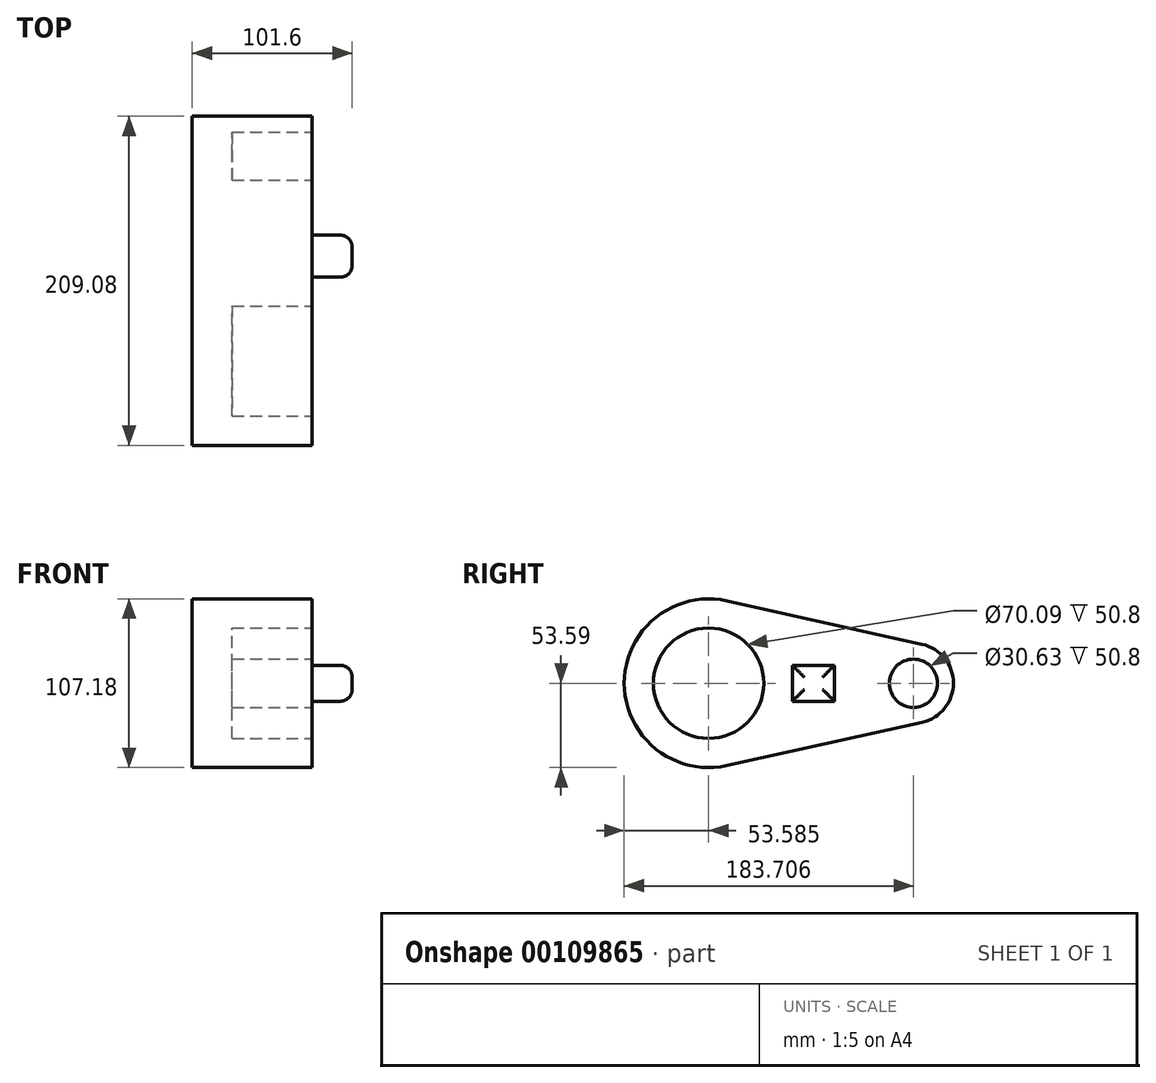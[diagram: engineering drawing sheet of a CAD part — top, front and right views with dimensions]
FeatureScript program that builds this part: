
annotation { "Feature Type Name" : "Feature", "Feature Type Description" : "" }
export const myFeature = defineFeature(function(context is Context, id is Id, definition is map)
    precondition{}
    {
        {
            var Q0;
            Q0=qCreatedBy(makeId("Right.planeOp"),FACE);
            var sketch = newSketch(context, id + "F0", { "sketchPlane" : qUnion([Q0])});
            skCircle(sketch, "E0", {"center": v(-66.59, 0) * mm, "radius": 53.59 * mm});
            skCircle(sketch, "E1", {"center": v(63.5, 0) * mm, "radius": 25.4 * mm});
            skLineSegment(sketch, "E2", {"start": v(-54.97, 52.32) * mm, "end": v(69, 24.8) * mm});
            skLineSegment(sketch, "E3", {"start": v(-54.97, -52.32) * mm, "end": v(69, -24.8) * mm});
            skSolve(sketch);
        }
        {
            var Q0;
            Q0 = qSketchRegion(id + "F0", true);
            extrude(context, id + "F1", {"entities" : qUnion([Q0]), "depth" : 76.2 * mm});
        }
        {
            var Q0;
            Q0=makeQuery(id+"F1.opExtrude","CAP_FACE",FACE,{"disambiguationData":[OSD([sQuery(id+"F0.wireOp",EDGE,"E0"),sQuery(id+"F0.wireOp",EDGE,"E1"),sQuery(id+"F0.wireOp",EDGE,"E2"),sQuery(id+"F0.wireOp",EDGE,"E3")])],"isStart":false});
            var sketch = newSketch(context, id + "F2", { "sketchPlane" : qUnion([Q0])});
            skCircle(sketch, "E4", {"center": v(-66.59, 0) * mm, "radius": 35.04 * mm});
            skSolve(sketch);
        }
        {
            var Q0;
            Q0=makeQuery(id+"F2.imprint","IMPRINT",FACE,{"disambiguationData":[TD([[makeQuery(id+"F2.imprint","IMPRINT",EDGE,{"derivedFrom":sQuery(id+"F2.wireOp",EDGE,"E4")}),1.0]])]});
            extrude(context, id + "F3", {"entities" : qUnion([Q0]), "operationType" : NewBodyOperationType.REMOVE, "oppositeDirection" : true, "depth" : 50.8 * mm});
        }
        {
            var Q0;
            Q0=makeQuery(id+"F2.imprint","IMPRINT",FACE,{"disambiguationData":[TD([[makeQuery(id+"F2.imprint","IMPRINT",EDGE,{"derivedFrom":sQuery(id+"F2.wireOp",EDGE,"E4")}),-1.0]])]});
            var sketch = newSketch(context, id + "F4", { "sketchPlane" : qUnion([Q0])});
            skCircle(sketch, "E5", {"center": v(63.54, 0) * mm, "radius": 15.32 * mm});
            skSolve(sketch);
        }
        {
            var Q0;
            Q0 = qSketchRegion(id + "F4", true);
            extrude(context, id + "F5", {"entities" : qUnion([Q0]), "operationType" : NewBodyOperationType.REMOVE, "oppositeDirection" : true, "depth" : 50.8 * mm});
        }
        {
            var Q0;
            Q0=makeQuery(id+"F2.imprint","IMPRINT",FACE,{"disambiguationData":[TD([[makeQuery(id+"F2.imprint","IMPRINT",EDGE,{"derivedFrom":sQuery(id+"F2.wireOp",EDGE,"E4")}),-1.0]])]});
            var sketch = newSketch(context, id + "F6", { "sketchPlane" : qUnion([Q0])});
            skLineSegment(sketch, "E6.bottom", {"start": v(13.39, -11.46) * mm, "end": v(-13.39, -11.46) * mm});
            skLineSegment(sketch, "E6.top", {"start": v(13.39, 11.46) * mm, "end": v(-13.39, 11.46) * mm});
            skLineSegment(sketch, "E6.left", {"start": v(13.39, -11.46) * mm, "end": v(13.39, 11.46) * mm});
            skLineSegment(sketch, "E6.right", {"start": v(-13.39, -11.46) * mm, "end": v(-13.39, 11.46) * mm});
            skPoint(sketch, "E6.middle", {"position": v(0, 0) * mm});
            skSolve(sketch);
        }
        {
            var Q0;
            Q0 = qSketchRegion(id + "F6", true);
            extrude(context, id + "F7", {"entities" : qUnion([Q0]), "operationType" : NewBodyOperationType.ADD, "depth" : 25.4 * mm});
        }
        {
            var Q0;
            Q0=makeQuery(id+"F7.opExtrude","CAP_FACE",FACE,{"disambiguationData":[OSD([sQuery(id+"F6.wireOp",EDGE,"E6.bottom"),sQuery(id+"F6.wireOp",EDGE,"E6.top"),sQuery(id+"F6.wireOp",EDGE,"E6.left"),sQuery(id+"F6.wireOp",EDGE,"E6.right")])],"isStart":false});
            fillet(context, id + "F8", {"entities" : qUnion([Q0]), "radius" : 7.62 * mm, "tangentPropagation" : true, "allowEdgeOverflow" : false});
        }
    });
